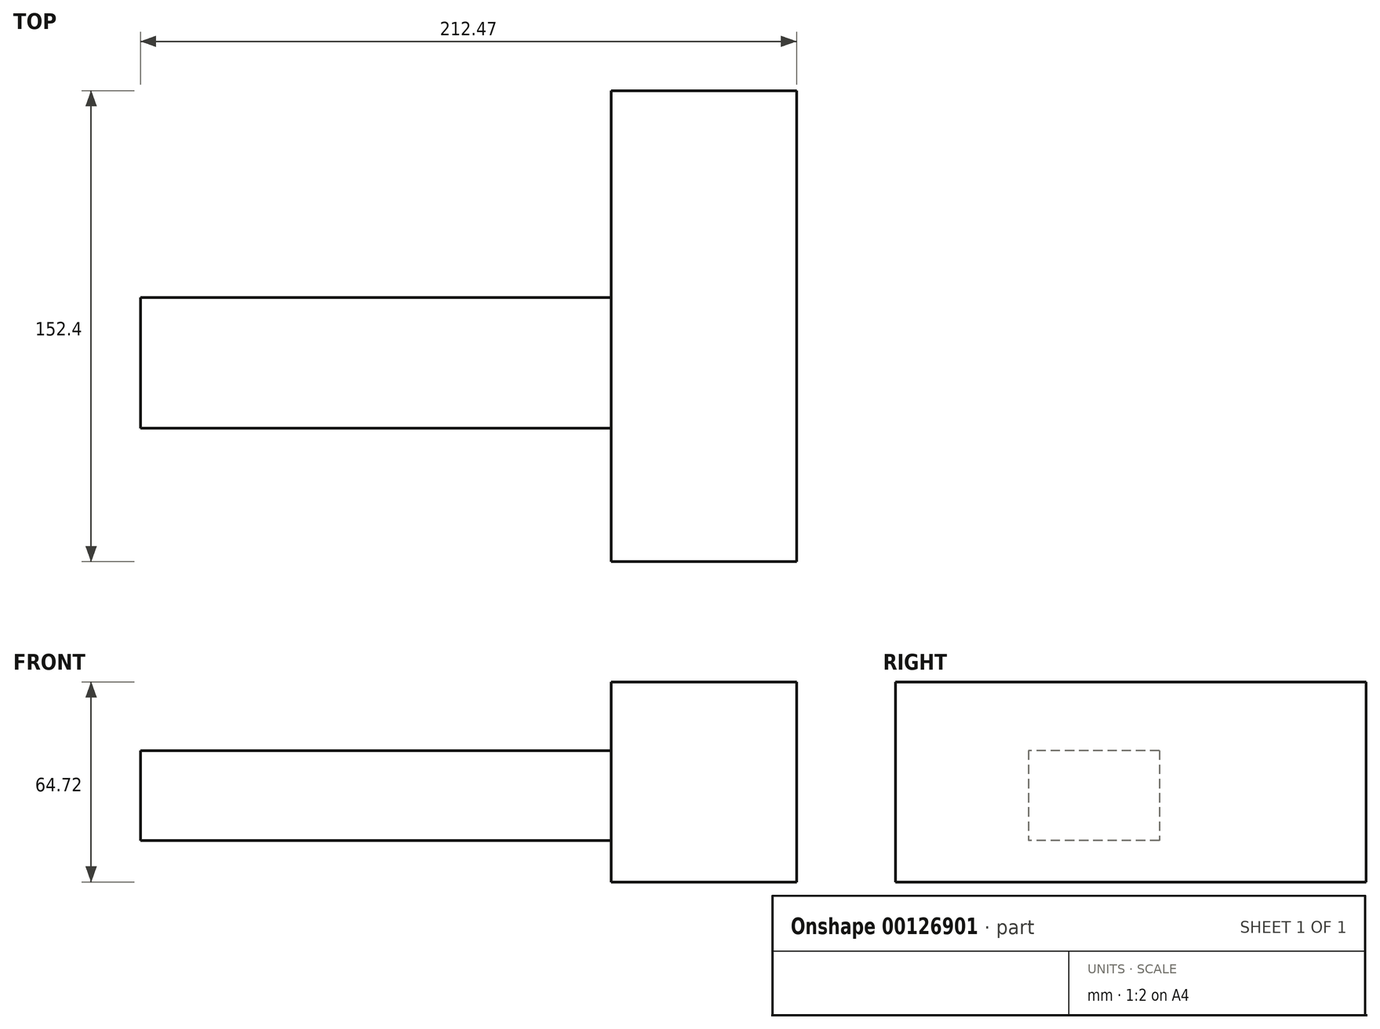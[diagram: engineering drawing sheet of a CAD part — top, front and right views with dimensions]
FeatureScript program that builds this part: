
annotation { "Feature Type Name" : "Feature", "Feature Type Description" : "" }
export const myFeature = defineFeature(function(context is Context, id is Id, definition is map)
    precondition{}
    {
        {
            var Q0;
            Q0=qCreatedBy(makeId("Front.planeOp"),FACE);
            var sketch = newSketch(context, id + "F0", { "sketchPlane" : qUnion([Q0])});
            skLineSegment(sketch, "E0.bottom", {"start": v(-20.75, 28.95) * mm, "end": v(39.32, 28.95) * mm});
            skLineSegment(sketch, "E0.top", {"start": v(-20.75, -35.77) * mm, "end": v(39.32, -35.77) * mm});
            skLineSegment(sketch, "E0.left", {"start": v(-20.75, 28.95) * mm, "end": v(-20.75, -35.77) * mm});
            skLineSegment(sketch, "E0.right", {"start": v(39.32, 28.95) * mm, "end": v(39.32, -35.77) * mm});
            skSolve(sketch);
        }
        {
            var Q0;
            Q0=makeQuery(id+"F0.imprint","IMPRINT",FACE,{"disambiguationData":[TD([[makeQuery(id+"F0.imprint","IMPRINT",EDGE,{"derivedFrom":sQuery(id+"F0.wireOp",EDGE,"E0.bottom")}),-1.0]])]});
            extrude(context, id + "F1", {"entities" : qUnion([Q0]), "depth" : 152.4 * mm});
        }
        {
            var Q0;
            Q0=makeQuery(id+"F1.opExtrude","SWEPT_FACE",FACE,{"disambiguationData":[OSD([sQuery(id+"F0.wireOp",EDGE,"E0.left")])]});
            var sketch = newSketch(context, id + "F2", { "sketchPlane" : qUnion([Q0])});
            skLineSegment(sketch, "E1.bottom", {"start": v(66.9, 6.78) * mm, "end": v(109.26, 6.78) * mm});
            skLineSegment(sketch, "E1.top", {"start": v(66.9, -22.3) * mm, "end": v(109.26, -22.3) * mm});
            skLineSegment(sketch, "E1.left", {"start": v(66.9, 6.78) * mm, "end": v(66.9, -22.3) * mm});
            skLineSegment(sketch, "E1.right", {"start": v(109.26, 6.78) * mm, "end": v(109.26, -22.3) * mm});
            skSolve(sketch);
        }
        {
            var Q0;
            Q0=makeQuery(id+"F2.imprint","IMPRINT",FACE,{"disambiguationData":[TD([[makeQuery(id+"F2.imprint","IMPRINT",EDGE,{"derivedFrom":sQuery(id+"F2.wireOp",EDGE,"E1.bottom")}),-1.0]])]});
            extrude(context, id + "F3", {"entities" : qUnion([Q0]), "operationType" : NewBodyOperationType.ADD, "depth" : 152.4 * mm});
        }
    });
